# Revit family: 0030379
name_source: partatom
category: Lighting Fixtures
revit_build: Autodesk Revit 2017 (Build: 20190507_1515(x64)
units: mm (PartAtom-declared; Revit-internal decimal feet)

## family parameters
Cut with Voids When Loaded = No
Host = Face
Light Source = Yes
OmniClass Number = 23.80.70.00
OmniClass Title = Lighting
Part Type = Normal
Room Calculation Point = No
Round Connector Dimension = Use Diameter
Shared = No

## types (1)
- 0030379 START DOWNLIGHT 90 IP44 830LM 830 DIM
    Apparent Load = 8 VA
    Assembly Code = D5020200
    AssetType = Fixed
    ClassificationName = Uniclass2015
    ClassificationValue = EF_70_80
    Color Filter = 16777215
    Cost = 0 $
    Default Elevation = 1219 mm
    Description = A ceiling recessed LED downlight IP44 (from the front) with phase dimmable driver, perfect where limited ceiling void is available with only 38mm product depth and 90mm cutout. The polycarbonate diffuser allows for a wider light distribution and increased spacings between luminiares. Loop in loop out connector allows for quick installation. Die-cast aluminium body, 830LM, 7.8W, 106lm/W, 3000K, Driver Current: 250mA, CRI80, 80° beam angle, IP44 from the front, IK07, 50,000 hrs (L70), (HxW) 38x109mm, 6 step MacAdam ellipse, Class 2, 220-240V, energy class: A++, A+, A
    DiameterRecess_SYL = 216 mm  [stored 0.708661 ft]
    DiameterTop_SYL = 105 mm  [stored 0.344488 ft]
    Diameter_SYL = 240 mm  [stored 0.787402 ft]
    Dimming Lamp Color Temperature Shift = <None>
    DocumentationLiterature = http://www.sylvania-lighting.com
    DurationUnit = hours
    ElectricShockClassification = Class II
    Emit Shape Visible in Rendering = No
    Emit from Circle Diameter = 64 mm  [stored 0.209974 ft]
    ExpectedLife = 50000
    Height_SYL = 62 mm  [stored 0.203412 ft]
    IfcExportAs = IfcLightFixtureType
    IfcExportType = IfcLightFixtureType
    ImpactProtectionIndex = IK07
    IngressProtection = IP44/20
    InputNominalFrequency = 50/60 Hz
    InputVoltage = 220-240 V AC
    Keynote = 16500
    Lamp = LED
    LampColourRenderingIndex = 80
    LampColourTemperature = 3000 K
    LampNominalLuminous = 830 lm
    LampsType = LED
    LuminousEfficacy = 106 lm/W
    Manufacturer = Feilo Sylvania
    ManufacturerName = Feilo Sylvania
    Material = aluminium housing, pc polycarbonate diffuser
    Material_1_SYL = Trim-Sylvania-STARTDownlight-White
    Material_2_SYL = Diffuser-Sylvania-STARTDownlight
    Material_3_SYL = Top-Sylvania-STARTDownlight
    Material_4_SYL = LED-Sylvania-STARTDownlight
    Model = START Downlight 90 IP44 830Lm 830 DIM
    ModelNumber = 0030379
    ModelReference = START Downlight 90 IP44 830Lm 830 DIM
    Name = START Downlight 90 IP44 830Lm 830 DIM
    NominalDepth = 109 mm  [stored 0.357612 ft]
    NominalHeight = 38 mm  [stored 0.124672 ft]
    NominalLength = 109 mm  [stored 0.357612 ft]
    Photometric Web File = 0030379.ies
    PowerConsumption = 7.8 W
    PowerFactor = 0.9
    RadiusTop_SYL = 120 mm  [stored 0.393701 ft]
    Tilt Angle = -90.00°
    Type Image = <None>
    TypeName = START Downlight 90 IP44 830Lm 830 DIM
    URL = http://www.sylvania-lighting.com
    Voltage = 230 V
    Weight = 5.22 kg

note: [stored X ft] marks values corroborated as IEEE doubles in the binary element streams (Revit-internal decimal feet)

## geometry (parser evidence)
native form markers: Sweep x2
no freeform markers — native parametric forms only
